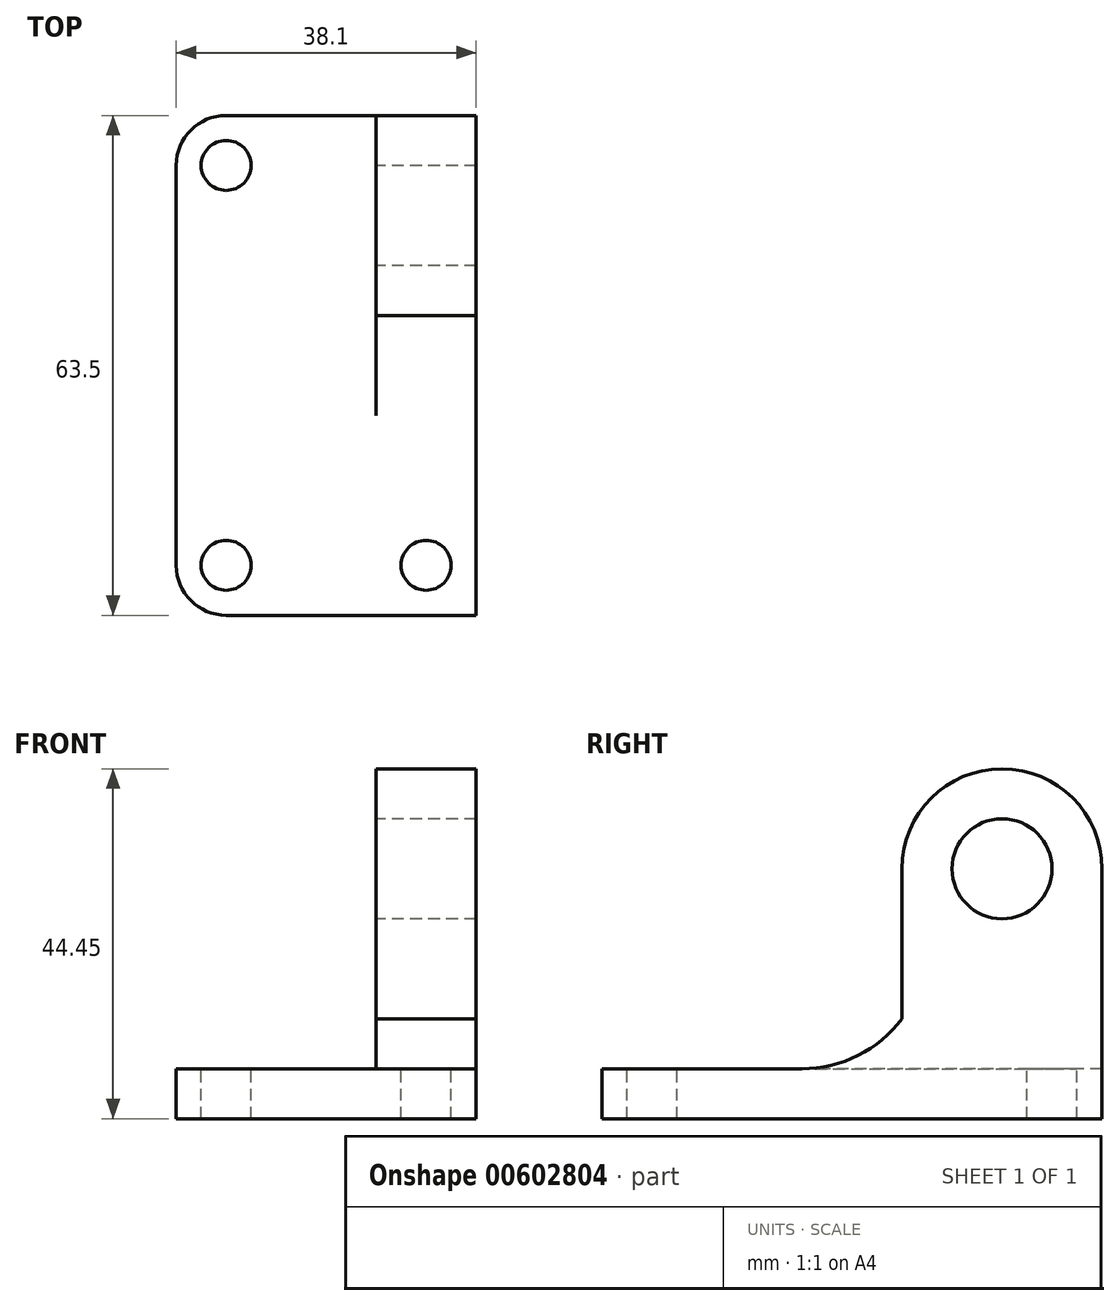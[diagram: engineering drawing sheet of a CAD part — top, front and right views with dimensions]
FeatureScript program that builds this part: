
annotation { "Feature Type Name" : "Feature", "Feature Type Description" : "" }
export const myFeature = defineFeature(function(context is Context, id is Id, definition is map)
    precondition{}
    {
        {
            var Q0;
            Q0=qCreatedBy(makeId("Top.planeOp"),FACE);
            var sketch = newSketch(context, id + "F0", { "sketchPlane" : qUnion([Q0])});
            skLineSegment(sketch, "E0", {"start": v(0, 0) * mm, "end": v(0, 63.5) * mm});
            skLineSegment(sketch, "E1", {"start": v(0, 63.5) * mm, "end": v(38.1, 63.5) * mm});
            skLineSegment(sketch, "E2", {"start": v(38.1, 63.5) * mm, "end": v(38.1, 0) * mm});
            skLineSegment(sketch, "E3", {"start": v(38.1, 0) * mm, "end": v(0, 0) * mm});
            skSolve(sketch);
        }
        {
            var Q0;
            Q0=makeQuery(id+"F0.imprint","IMPRINT",FACE,{"disambiguationData":[TD([[makeQuery(id+"F0.imprint","IMPRINT",EDGE,{"derivedFrom":sQuery(id+"F0.wireOp",EDGE,"E0")}),-1.0]])]});
            extrude(context, id + "F1", {"entities" : qUnion([Q0]), "depth" : 44.45 * mm, "offsetDistance" : 25.4 * mm});
        }
        {
            var Q0;
            Q0=makeQuery(id+"F1.opExtrude","CAP_FACE",FACE,{"disambiguationData":[OSD([sQuery(id+"F0.wireOp",EDGE,"E0"),sQuery(id+"F0.wireOp",EDGE,"E1"),sQuery(id+"F0.wireOp",EDGE,"E2"),sQuery(id+"F0.wireOp",EDGE,"E3")])],"isStart":false});
            var sketch = newSketch(context, id + "F2", { "sketchPlane" : qUnion([Q0])});
            skLineSegment(sketch, "E4", {"start": v(25.4, 63.5) * mm, "end": v(25.4, 25.4) * mm});
            skLineSegment(sketch, "E5", {"start": v(25.4, 25.4) * mm, "end": v(38.1, 25.4) * mm});
            skLineSegment(sketch, "E6", {"start": v(38.1, 25.4) * mm, "end": v(38.1, 63.5) * mm});
            skLineSegment(sketch, "E7", {"start": v(38.1, 63.5) * mm, "end": v(25.4, 63.5) * mm});
            skSolve(sketch);
        }
        {
            var Q0;
            {var subQ3=sQuery(id+"F2.wireOp",EDGE,"E4");Q0=makeQuery(id+"F2.imprint","IMPRINT",FACE,{"disambiguationData":[TD([[makeQuery(id+"F2.imprint","IMPRINT",EDGE,{"derivedFrom":subQ3}),-1.0]])]});}
            extrude(context, id + "F3", {"entities" : qUnion([Q0]), "operationType" : NewBodyOperationType.REMOVE, "oppositeDirection" : true, "depth" : 38.1 * mm, "offsetDistance" : 25.4 * mm});
        }
        {
            var Q0;
            Q0=makeQuery(id+"F3.boolean.opBoolean","COPY",FACE,{"derivedFrom":makeQuery(id+"F3.opExtrude","SWEPT_FACE",FACE,{"disambiguationData":[OSD([sQuery(id+"F2.wireOp",EDGE,"E4")])]})});
            var sketch = newSketch(context, id + "F4", { "sketchPlane" : qUnion([Q0])});
            skLineSegment(sketch, "E8", {"start": v(-63.5, 6.35) * mm, "end": v(-63.5, 44.45) * mm});
            skLineSegment(sketch, "E9", {"start": v(-63.5, 44.45) * mm, "end": v(-25.4, 44.45) * mm});
            skLineSegment(sketch, "E10", {"start": v(-25.4, 44.45) * mm, "end": v(-25.4, 6.35) * mm});
            skLineSegment(sketch, "E11", {"start": v(-25.4, 6.35) * mm, "end": v(-63.5, 6.35) * mm});
            skCircle(sketch, "E12", {"center": v(-50.8, 31.75) * mm, "radius": 12.7 * mm});
            skLineSegment(sketch, "E13", {"start": v(-50.8, 31.75) * mm, "end": v(-38.1, 31.75) * mm});
            skLineSegment(sketch, "E14", {"start": v(-38.1, 44.45) * mm, "end": v(-38.1, 12.7) * mm});
            skArc(sketch, "E15", {"start": v(-38.1, 12.7) * mm, "mid": v(-32.5, 8.03) * mm, "end": v(-25.4, 6.35) * mm});
            skSolve(sketch);
        }
        {
            var Q0;
            {var subQ0=sQuery(id+"F4.wireOp",EDGE,"E9");var subQ1=sQuery(id+"F4.wireOp",EDGE,"E8");var subQ2=makeQuery(id+"F4.imprint","INTERSECT",VERTEX,{"derivedFrom":[subQ1,subQ0]});Q0=makeQuery(id+"F4.imprint","IMPRINT",FACE,{"disambiguationData":[TD([[makeQuery(id+"F4.imprint","IMPRINT",EDGE,{"disambiguationData":[TD([[subQ2,1.0]])],"derivedFrom":subQ1}),-1.0]])]});}
            extrude(context, id + "F5", {"entities" : qUnion([Q0]), "operationType" : NewBodyOperationType.REMOVE, "oppositeDirection" : true, "depth" : 25.4 * mm, "offsetDistance" : 25.4 * mm});
        }
        {
            var Q0;
            Q0=makeQuery(id+"F3.boolean.opBoolean","COPY",FACE,{"derivedFrom":makeQuery(id+"F3.opExtrude","SWEPT_FACE",FACE,{"disambiguationData":[OSD([sQuery(id+"F2.wireOp",EDGE,"E4")])]})});
            var sketch = newSketch(context, id + "F6", { "sketchPlane" : qUnion([Q0])});
            skLineSegment(sketch, "E16.0.0", {"start": v(-25.4, 44.45) * mm, "end": v(-50.8, 44.45) * mm});
            skArc(sketch, "E16.0.1", {"start": v(-50.8, 44.45) * mm, "mid": v(-59.78, 40.73) * mm, "end": v(-63.5, 31.75) * mm});
            skLineSegment(sketch, "E16.0.2", {"start": v(-63.5, 31.75) * mm, "end": v(-63.5, 6.35) * mm});
            skLineSegment(sketch, "E16.0.3", {"start": v(-63.5, 6.35) * mm, "end": v(-25.4, 6.35) * mm});
            skLineSegment(sketch, "E16.0.4", {"start": v(-25.4, 6.35) * mm, "end": v(-25.4, 44.45) * mm});
            skSolve(sketch);
        }
        {
            var Q0;
            {var subQ5=sQuery(id+"F4.wireOp",EDGE,"E10");Q0=makeQuery(id+"F4.imprint","IMPRINT",FACE,{"disambiguationData":[TD([[makeQuery(id+"F4.imprint","IMPRINT",EDGE,{"derivedFrom":subQ5}),1.0]])]});}
            var Q1;
            {var subQ0=sQuery(id+"F4.wireOp",EDGE,"E14");var subQ1=sQuery(id+"F4.wireOp",EDGE,"E9");var subQ2=makeQuery(id+"F4.imprint","INTERSECT",VERTEX,{"derivedFrom":[subQ1,subQ0]});Q1=makeQuery(id+"F4.imprint","IMPRINT",FACE,{"disambiguationData":[TD([[makeQuery(id+"F4.imprint","IMPRINT",EDGE,{"disambiguationData":[TD([[subQ2,1.0]])],"derivedFrom":subQ1}),-1.0]])]});}
            extrude(context, id + "F7", {"entities" : qUnion([Q0, Q1]), "operationType" : NewBodyOperationType.REMOVE, "oppositeDirection" : true, "depth" : 25.4 * mm, "offsetDistance" : 25.4 * mm});
        }
        {
            var Q0;
            Q0=makeQuery(id+"F6.imprint","IMPRINT",FACE,{"disambiguationData":[TD([[makeQuery(id+"F6.imprint","IMPRINT",EDGE,{"derivedFrom":sQuery(id+"F6.wireOp",EDGE,"E16.0.0")}),-1.0]])]});
            var sketch = newSketch(context, id + "F8", { "sketchPlane" : qUnion([Q0])});
            skPoint(sketch, "E17.0", {"position": v(-50.8, 31.75) * mm});
            skCircle(sketch, "E18", {"center": v(-50.8, 31.75) * mm, "radius": 6.35 * mm});
            skSolve(sketch);
        }
        {
            var Q0;
            Q0 = qSketchRegion(id + "F8", true);
            extrude(context, id + "F9", {"entities" : qUnion([Q0]), "operationType" : NewBodyOperationType.REMOVE, "oppositeDirection" : true, "depth" : 25.4 * mm, "offsetDistance" : 25.4 * mm});
        }
        {
            var Q0;
            Q0=makeQuery(id+"F3.boolean.opBoolean","COPY",FACE,{"derivedFrom":makeQuery(id+"F3.opExtrude","CAP_FACE",FACE,{"disambiguationData":[OSD([sQuery(id+"F0.wireOp",EDGE,"E0"),sQuery(id+"F0.wireOp",EDGE,"E1"),sQuery(id+"F0.wireOp",EDGE,"E2"),sQuery(id+"F0.wireOp",EDGE,"E3"),sQuery(id+"F2.wireOp",EDGE,"E4"),sQuery(id+"F2.wireOp",EDGE,"E5")])],"isStart":false})});
            var sketch = newSketch(context, id + "F10", { "sketchPlane" : qUnion([Q0])});
            skCircle(sketch, "E19", {"center": v(31.75, 6.35) * mm, "radius": 3.18 * mm});
            skCircle(sketch, "E20", {"center": v(6.35, 6.35) * mm, "radius": 3.18 * mm});
            skCircle(sketch, "E21", {"center": v(6.35, 57.15) * mm, "radius": 3.18 * mm});
            skSolve(sketch);
        }
        {
            var Q0;
            Q0=makeQuery(id+"F10.imprint","IMPRINT",FACE,{"disambiguationData":[TD([[makeQuery(id+"F10.imprint","IMPRINT",EDGE,{"derivedFrom":sQuery(id+"F10.wireOp",EDGE,"E19")}),1.0]])]});
            var Q1;
            Q1=makeQuery(id+"F10.imprint","IMPRINT",FACE,{"disambiguationData":[TD([[makeQuery(id+"F10.imprint","IMPRINT",EDGE,{"derivedFrom":sQuery(id+"F10.wireOp",EDGE,"E20")}),1.0]])]});
            var Q2;
            Q2=makeQuery(id+"F10.imprint","IMPRINT",FACE,{"disambiguationData":[TD([[makeQuery(id+"F10.imprint","IMPRINT",EDGE,{"derivedFrom":sQuery(id+"F10.wireOp",EDGE,"E21")}),1.0]])]});
            extrude(context, id + "F11", {"entities" : qUnion([Q0, Q1, Q2]), "operationType" : NewBodyOperationType.REMOVE, "oppositeDirection" : true, "depth" : 25.4 * mm, "offsetDistance" : 25.4 * mm});
        }
        {
            var Q0;
            Q0=makeQuery(id+"F3.boolean.opBoolean","COPY",FACE,{"derivedFrom":makeQuery(id+"F3.opExtrude","CAP_FACE",FACE,{"disambiguationData":[OSD([sQuery(id+"F0.wireOp",EDGE,"E0"),sQuery(id+"F0.wireOp",EDGE,"E1"),sQuery(id+"F0.wireOp",EDGE,"E2"),sQuery(id+"F0.wireOp",EDGE,"E3"),sQuery(id+"F2.wireOp",EDGE,"E4"),sQuery(id+"F2.wireOp",EDGE,"E5")])],"isStart":false})});
            var sketch = newSketch(context, id + "F12", { "sketchPlane" : qUnion([Q0])});
            skCircle(sketch, "E22", {"center": v(6.35, 6.35) * mm, "radius": 6.35 * mm});
            skSolve(sketch);
        }
        {
            var Q0;
            {var subQ0=sQuery(id+"F12.wireOp",EDGE,"E22");var subQ1=makeQuery(id+"F3.boolean.opBoolean","COPY",EDGE,{"derivedFrom":makeQuery(id+"F3.opExtrude","CAP_EDGE",EDGE,{"disambiguationData":[OSD([sQuery(id+"F0.wireOp",EDGE,"E0")])],"isStart":false})});var subQ2=makeQuery(id+"F12.imprint","INTERSECT",VERTEX,{"derivedFrom":[subQ1,subQ0]});Q0=makeQuery(id+"F12.imprint","IMPRINT",FACE,{"disambiguationData":[TD([[makeQuery(id+"F12.imprint","IMPRINT",EDGE,{"disambiguationData":[TD([[subQ2,-1.0]])],"derivedFrom":subQ0}),-1.0]])]});}
            extrude(context, id + "F13", {"entities" : qUnion([Q0]), "operationType" : NewBodyOperationType.REMOVE, "oppositeDirection" : true, "depth" : 25.4 * mm, "offsetDistance" : 25.4 * mm});
        }
        {
            var Q0;
            Q0=makeQuery(id+"F3.boolean.opBoolean","COPY",FACE,{"derivedFrom":makeQuery(id+"F3.opExtrude","CAP_FACE",FACE,{"disambiguationData":[OSD([sQuery(id+"F0.wireOp",EDGE,"E0"),sQuery(id+"F0.wireOp",EDGE,"E1"),sQuery(id+"F0.wireOp",EDGE,"E2"),sQuery(id+"F0.wireOp",EDGE,"E3"),sQuery(id+"F2.wireOp",EDGE,"E4"),sQuery(id+"F2.wireOp",EDGE,"E5")])],"isStart":false})});
            var sketch = newSketch(context, id + "F14", { "sketchPlane" : qUnion([Q0])});
            skCircle(sketch, "E23", {"center": v(6.35, 57.15) * mm, "radius": 6.35 * mm});
            skSolve(sketch);
        }
        {
            var Q0;
            {var subQ0=sQuery(id+"F14.wireOp",EDGE,"E23");var subQ1=makeQuery(id+"F3.boolean.opBoolean","COPY",EDGE,{"derivedFrom":makeQuery(id+"F3.opExtrude","CAP_EDGE",EDGE,{"disambiguationData":[OSD([sQuery(id+"F0.wireOp",EDGE,"E1")])],"isStart":false})});var subQ2=makeQuery(id+"F14.imprint","INTERSECT",VERTEX,{"derivedFrom":[subQ1,subQ0]});Q0=makeQuery(id+"F14.imprint","IMPRINT",FACE,{"disambiguationData":[TD([[makeQuery(id+"F14.imprint","IMPRINT",EDGE,{"disambiguationData":[TD([[subQ2,-1.0]])],"derivedFrom":subQ0}),-1.0]])]});}
            extrude(context, id + "F15", {"entities" : qUnion([Q0]), "operationType" : NewBodyOperationType.REMOVE, "oppositeDirection" : true, "depth" : 25.4 * mm, "offsetDistance" : 25.4 * mm});
        }
    });
